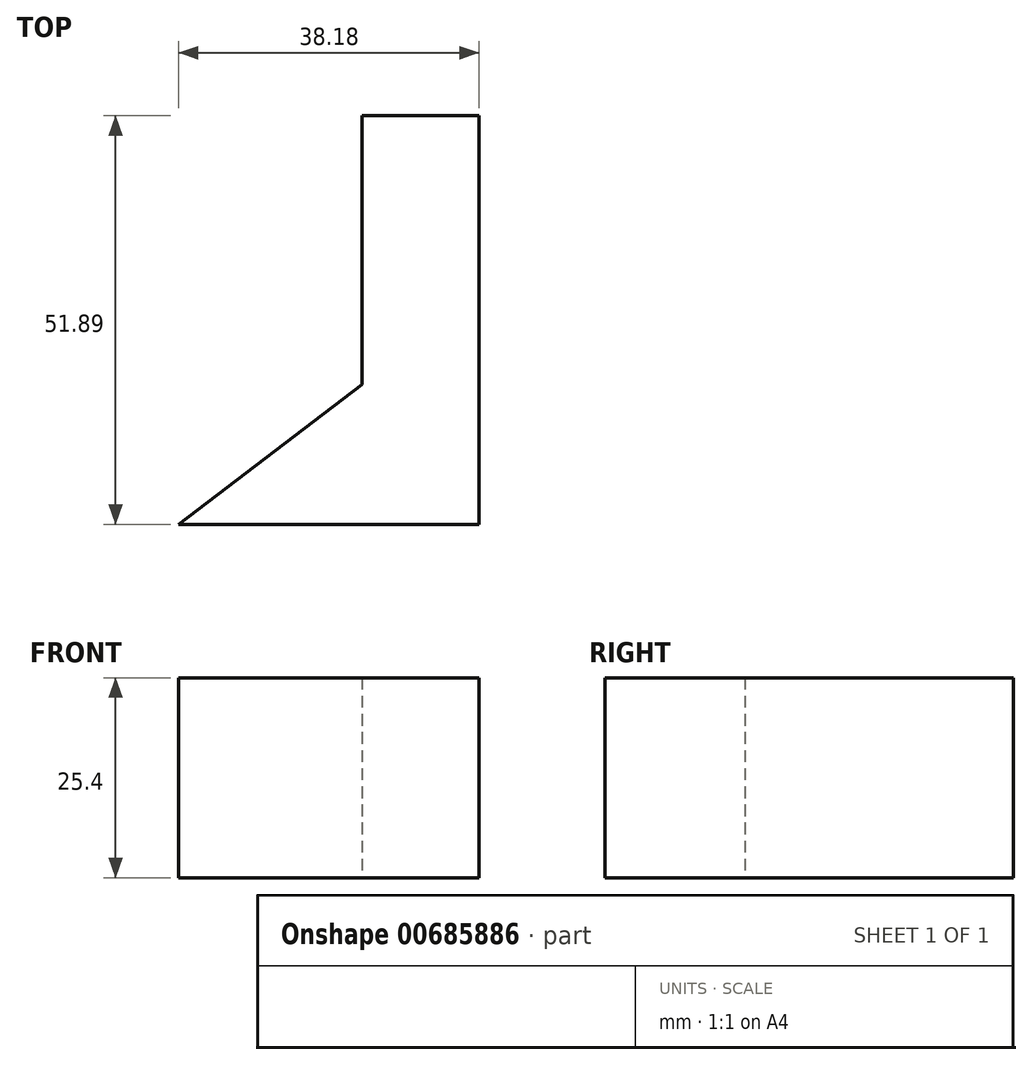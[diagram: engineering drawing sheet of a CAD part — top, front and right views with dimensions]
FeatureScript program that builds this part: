
annotation { "Feature Type Name" : "Feature", "Feature Type Description" : "" }
export const myFeature = defineFeature(function(context is Context, id is Id, definition is map)
    precondition{}
    {
        {
            var Q0;
            Q0=qCreatedBy(makeId("Top.planeOp"),FACE);
            var sketch = newSketch(context, id + "F0", { "sketchPlane" : qUnion([Q0])});
            skLineSegment(sketch, "E0", {"start": v(-38.18, 0) * mm, "end": v(0, 0) * mm});
            skLineSegment(sketch, "E1", {"start": v(0, 0) * mm, "end": v(0, 51.9) * mm});
            skLineSegment(sketch, "E2", {"start": v(0, 51.9) * mm, "end": v(-14.9, 51.9) * mm});
            skLineSegment(sketch, "E3", {"start": v(-14.9, 51.9) * mm, "end": v(-14.9, 17.76) * mm});
            skLineSegment(sketch, "E4", {"start": v(-14.9, 17.76) * mm, "end": v(-38.18, 0) * mm});
            skSolve(sketch);
        }
        {
            var Q0;
            Q0 = qSketchRegion(id + "F0", true);
            extrude(context, id + "F1", {"entities" : qUnion([Q0]), "depth" : 25.4 * mm, "offsetDistance" : 25.4 * mm});
        }
    });
